# Revit family: GI
name_source: partatom
category: Mechanical Equipment
units: mm (PartAtom-declared; Revit-internal decimal feet)

## family parameters
Always vertical = Yes
Cut with Voids When Loaded = No
Part Type = Normal
Room Calculation Point = No
Round Connector Dimension = Use Diameter
Shared = No
Work Plane-Based = No

## types (1)
- GI
    -HL/2 = -30"
    -hw/2 = -21 19/32"
    0 = 0"
    1.25 = 1 1/4"
    1.5 = 1 1/2"
    2" = 2"
    2.75 = 2 3/4"
    GI_Throat_Length = 36"
    GI_Throat_Width = 24"
    H = 19 1/16"
    H/10 = 1 29/32"
    H/4 = 9 5/8"
    H/6 = 3 3/16"
    HL_/2 = 30"
    HW_/2 = 21 19/32"
    HoodArea = 18 SF
    HoodLength = 60"
    HoodWidth = 43 3/16"
    Manufacturer = Loren Cook Company
    Model = GI
    ONE EIGTH = 1/8"
    TL_/2 = 18"
    TW_/2 = 12"
    Type Comments = Aluminum Intake Ventilator
    URL = www.lorencook.com
    hoodwidthB = 43 3/16"
    hw = 43 3/16"
    nhp = 682 15/16"
    qtyhoodpanel = 5
    ratio = 2
    tempA = 60"
    tempB = 60"
    tl+5.5/2 = 20 3/4"
    tlplus5.5 = 41 1/2"
    tw+5.5/2 = 14 3/4"
    twplus5.5 = 29 1/2"

## geometry (parser evidence)
native form markers: Sweep x2
no freeform markers — native parametric forms only
